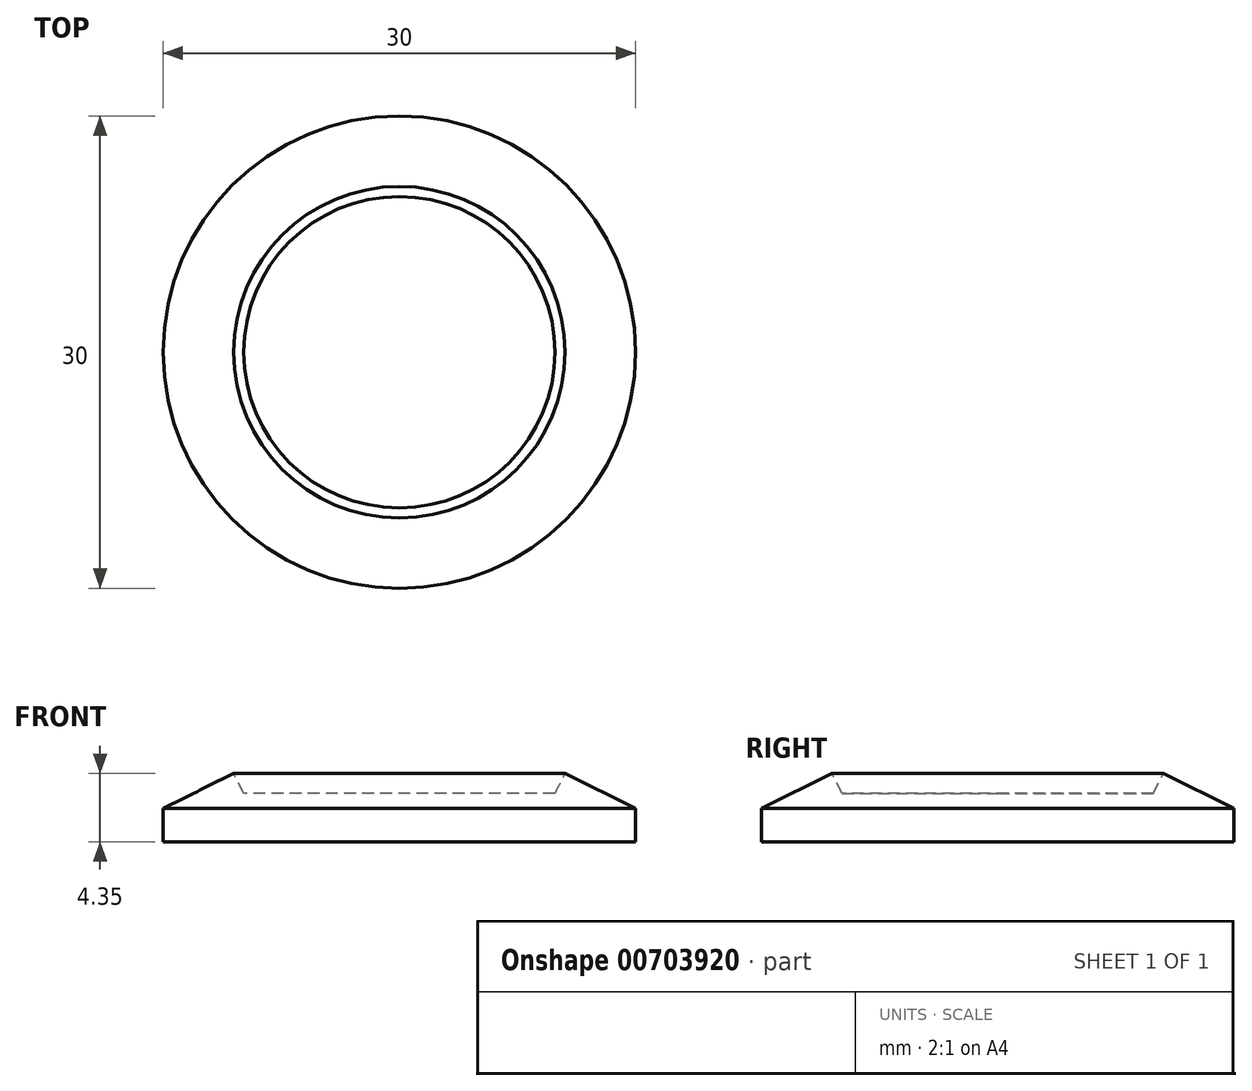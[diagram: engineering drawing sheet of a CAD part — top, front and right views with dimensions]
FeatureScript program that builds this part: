
annotation { "Feature Type Name" : "Feature", "Feature Type Description" : "" }
export const myFeature = defineFeature(function(context is Context, id is Id, definition is map)
    precondition{}
    {
        {
            var Q0;
            Q0=qCreatedBy(makeId("Front.planeOp"),FACE);
            var sketch = newSketch(context, id + "F0", { "sketchPlane" : qUnion([Q0])});
            skLineSegment(sketch, "E0", {"start": v(0, 9.59) * mm, "end": v(0, -2.57) * mm, "construction": true});
            skLineSegment(sketch, "E1", {"start": v(0, 8.62) * mm, "end": v(15, 1.12) * mm, "construction": true});
            skLineSegment(sketch, "E2", {"start": v(0, -1) * mm, "end": v(13.94, -1) * mm});
            skLineSegment(sketch, "E3", {"start": v(13.94, -1) * mm, "end": v(15.45, 2.01) * mm});
            skLineSegment(sketch, "E4", {"start": v(15.45, 2.01) * mm, "end": v(10.84, 3.98) * mm});
            skLineSegment(sketch, "E5", {"start": v(10.84, 3.98) * mm, "end": v(9.89, 2.07) * mm});
            skLineSegment(sketch, "E6", {"start": v(9.89, 2.07) * mm, "end": v(0, 2.07) * mm});
            skPoint(sketch, "E7", {"position": v(14.44, 0) * mm});
            skPoint(sketch, "E8", {"position": v(15, 1.12) * mm});
            skPoint(sketch, "E9", {"position": v(10.14, 2.57) * mm});
            skLineSegment(sketch, "E10", {"start": v(0, 8.62) * mm, "end": v(15.45, 2.01) * mm, "construction": true});
            skLineSegment(sketch, "E11", {"start": v(0, 8.62) * mm, "end": v(14.44, 0) * mm, "construction": true});
            skPoint(sketch, "E12", {"position": v(10.53, 3.35) * mm});
            skLineSegment(sketch, "E13", {"start": v(0, 2.07) * mm, "end": v(0, -1) * mm});
            skSolve(sketch);
        }
        {
            var Q0;
            Q0=qCreatedBy(makeId("Front.planeOp"),FACE);
            var sketch = newSketch(context, id + "F1", { "sketchPlane" : qUnion([Q0])});
            skLineSegment(sketch, "E14.0", {"start": v(9.89, 2.07) * mm, "end": v(0, 2.07) * mm});
            skLineSegment(sketch, "E15.0", {"start": v(10.53, 3.35) * mm, "end": v(9.89, 2.07) * mm});
            skLineSegment(sketch, "E16.0", {"start": v(10.53, 3.35) * mm, "end": v(15, 1.12) * mm});
            skLineSegment(sketch, "E17.0", {"start": v(13.94, -1) * mm, "end": v(15, 1.12) * mm});
            skLineSegment(sketch, "E18.0", {"start": v(0, -1) * mm, "end": v(13.94, -1) * mm});
            skPoint(sketch, "E19.orphan", {"position": v(0, 8.62) * mm});
            skPoint(sketch, "E20.orphan", {"position": v(15.45, 2.01) * mm});
            skLineSegment(sketch, "E21.0", {"start": v(0, 2.07) * mm, "end": v(0, -1) * mm});
            skSolve(sketch);
        }
        {
            var Q0;
            Q0=qSketchRegion(id+"F1",true);
            var Q1;
            Q1=sQuery(id+"F0.wireOp",EDGE,"E0");
            revolve(context, id + "F2", {"entities" : qUnion([Q0]), "axis" : qUnion([Q1]), "revolveType" : RevolveType.FULL});
        }
        {
            var Q0;
            Q0=makeQuery(id+"F2.opRevolve","SWEPT_FACE",FACE,{"disambiguationData":[OSD([sQuery(id+"F1.wireOp",EDGE,"E18.0")])]});
            var sketch = newSketch(context, id + "F3", { "sketchPlane" : qUnion([Q0])});
            skCircle(sketch, "E22.0", {"center": v(0, 0) * mm, "radius": 15 * mm});
            skCircle(sketch, "E23.0", {"center": v(0, 0) * mm, "radius": 13.94 * mm});
            skSolve(sketch);
        }
        {
            var Q0;
            Q0=qSketchRegion(id+"F3",true);
            extrude(context, id + "F4", {"entities" : qUnion([Q0]), "operationType" : NewBodyOperationType.ADD, "endBound" : BoundingType.UP_TO_NEXT, "oppositeDirection" : true, "depth" : 25 * mm, "offsetDistance" : 25 * mm});
        }
    });
